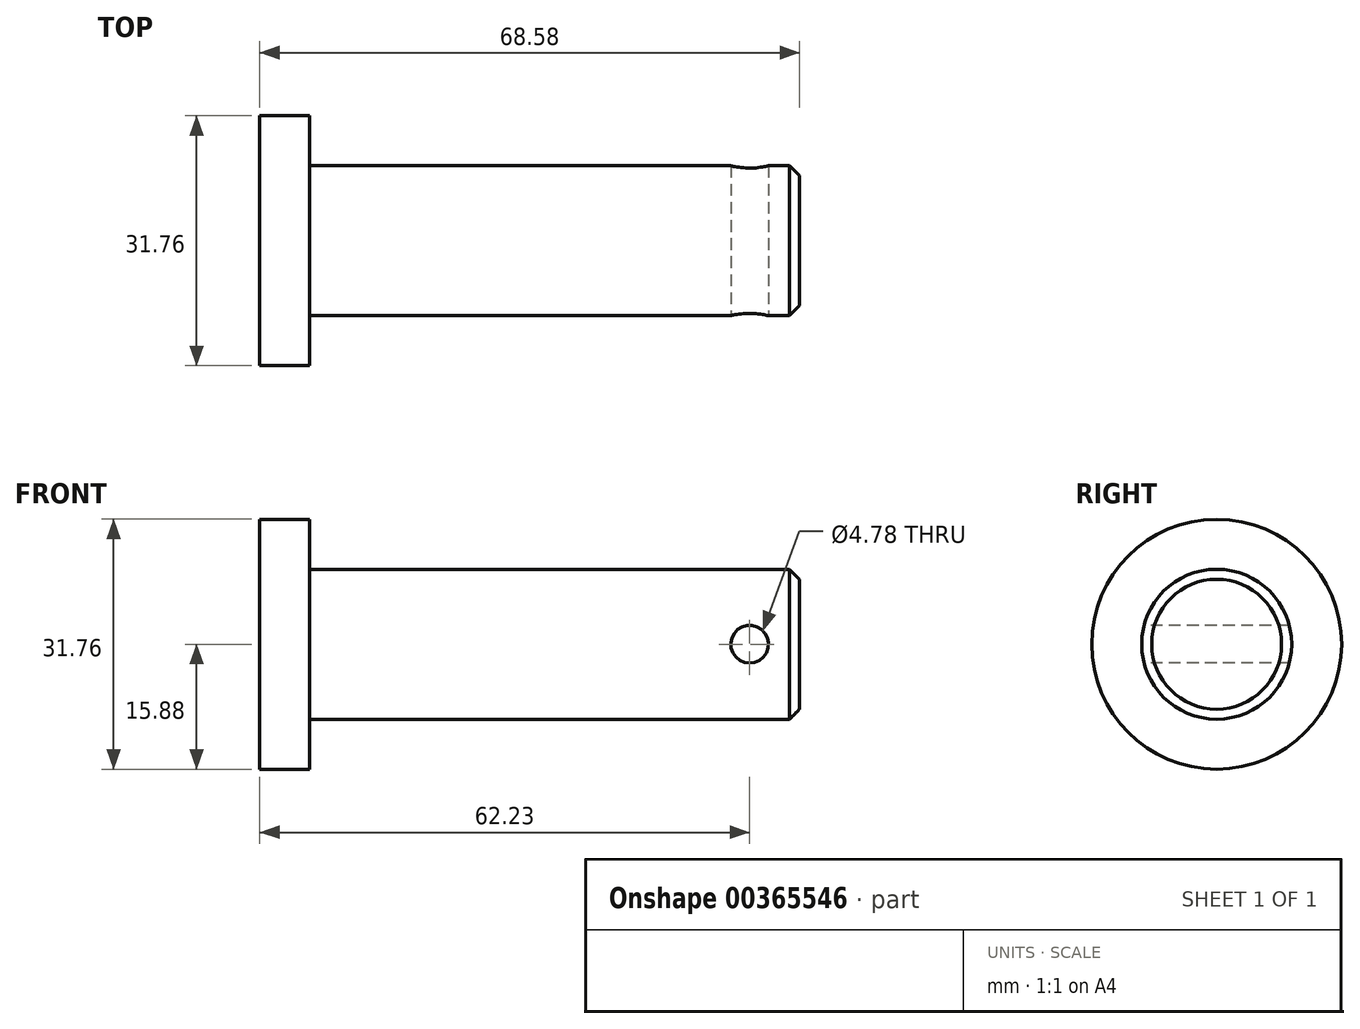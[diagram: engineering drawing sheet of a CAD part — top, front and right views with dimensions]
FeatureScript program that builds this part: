
annotation { "Feature Type Name" : "Feature", "Feature Type Description" : "" }
export const myFeature = defineFeature(function(context is Context, id is Id, definition is map)
    precondition{}
    {
        {
            var Q0;
            Q0=qCreatedBy(makeId("Right.planeOp"),FACE);
            var sketch = newSketch(context, id + "F0", { "sketchPlane" : qUnion([Q0])});
            skCircle(sketch, "E0", {"center": v(0, 0) * mm, "radius": 15.88 * mm});
            skSolve(sketch);
        }
        {
            var Q0;
            Q0=makeQuery(id+"F0.imprint","IMPRINT",FACE,{"disambiguationData":[TD([[makeQuery(id+"F0.imprint","IMPRINT",EDGE,{"derivedFrom":sQuery(id+"F0.wireOp",EDGE,"E0")}),1.0]])]});
            extrude(context, id + "F1", {"entities" : qUnion([Q0]), "depth" : 6.35 * mm});
        }
        {
            var Q0;
            Q0=makeQuery(id+"F1.opExtrude","CAP_FACE",FACE,{"disambiguationData":[OSD([sQuery(id+"F0.wireOp",EDGE,"E0")])],"isStart":false});
            var sketch = newSketch(context, id + "F2", { "sketchPlane" : qUnion([Q0])});
            skCircle(sketch, "E1", {"center": v(0, 0) * mm, "radius": 9.53 * mm});
            skSolve(sketch);
        }
        {
            var Q0;
            Q0 = qSketchRegion(id + "F2", true);
            extrude(context, id + "F3", {"entities" : qUnion([Q0]), "operationType" : NewBodyOperationType.ADD, "depth" : 62.23 * mm});
        }
        {
            var Q0;
            Q0=qCreatedBy(makeId("Front.planeOp"),FACE);
            var sketch = newSketch(context, id + "F4", { "sketchPlane" : qUnion([Q0])});
            skCircle(sketch, "E2", {"center": v(62.23, 0) * mm, "radius": 2.39 * mm});
            skSolve(sketch);
        }
        {
            var Q0;
            Q0 = qSketchRegion(id + "F4", true);
            extrude(context, id + "F5", {"entities" : qUnion([Q0]), "operationType" : NewBodyOperationType.REMOVE, "endBound" : BoundingType.SYMMETRIC, "oppositeDirection" : true, "depth" : 254 * mm});
        }
        {
            var Q0;
            Q0=makeQuery(id+"F3.opExtrude","CAP_EDGE",EDGE,{"disambiguationData":[OSD([sQuery(id+"F2.wireOp",EDGE,"E1")])],"isStart":false});
            chamfer(context, id + "F6", {"entities" : qUnion([Q0]), "chamferType" : ChamferType.OFFSET_ANGLE, "width" : 1.27 * mm, "oppositeDirection" : false, "angle" : 45 * degree, "tangentPropagation" : true});
        }
    });
